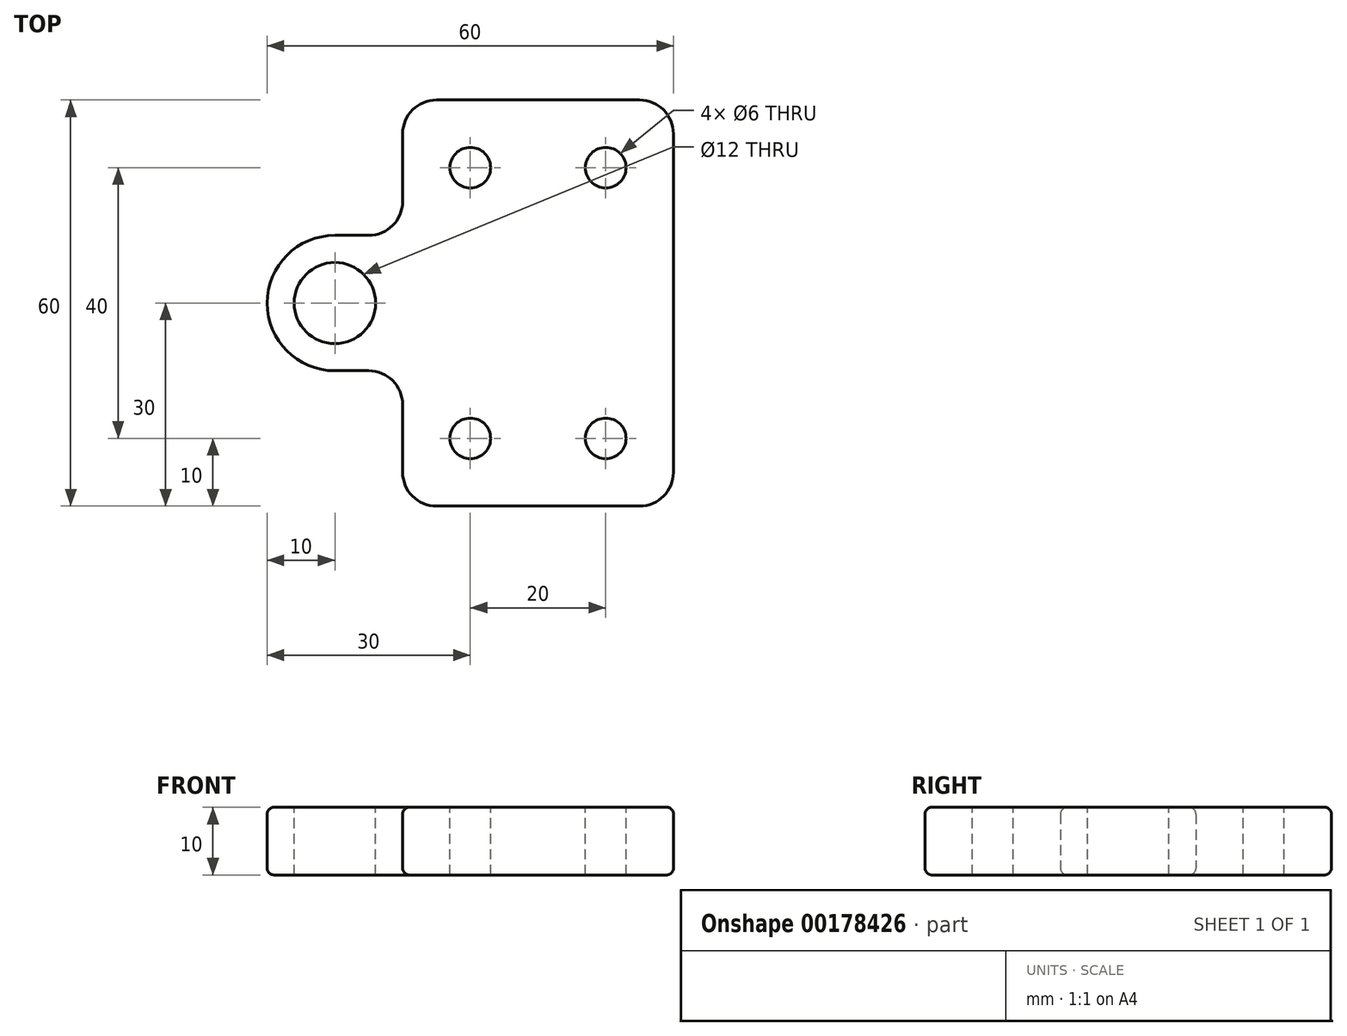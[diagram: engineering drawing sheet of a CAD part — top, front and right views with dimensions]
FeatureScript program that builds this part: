
annotation { "Feature Type Name" : "Feature", "Feature Type Description" : "" }
export const myFeature = defineFeature(function(context is Context, id is Id, definition is map)
    precondition{}
    {
        {
            var Q0;
            Q0=qCreatedBy(makeId("Top.planeOp"),FACE);
            var sketch = newSketch(context, id + "F0", { "sketchPlane" : qUnion([Q0])});
            skLineSegment(sketch, "E0.bottom", {"start": v(-20, 30) * mm, "end": v(20, 30) * mm});
            skLineSegment(sketch, "E0.top", {"start": v(-20, -30) * mm, "end": v(20, -30) * mm});
            skLineSegment(sketch, "E0.left", {"start": v(-20, 30) * mm, "end": v(-20, 10) * mm});
            skLineSegment(sketch, "E0.right", {"start": v(20, 30) * mm, "end": v(20, -30) * mm});
            skPoint(sketch, "E0.middle", {"position": v(0, 0) * mm});
            skPoint(sketch, "E1", {"position": v(-30, 0) * mm});
            skPoint(sketch, "E1.positionSnap0", {"position": v(-20, 0) * mm});
            skArc(sketch, "E2", {"start": v(-30, 10) * mm, "mid": v(-40, 0) * mm, "end": v(-30, -10) * mm});
            skLineSegment(sketch, "E3", {"start": v(-30, 10) * mm, "end": v(-20, 10) * mm});
            skLineSegment(sketch, "E4", {"start": v(-30, -10) * mm, "end": v(-20, -10) * mm});
            skLineSegment(sketch, "E5.trimOffspring", {"start": v(-20, -10) * mm, "end": v(-20, -30) * mm});
            skSolve(sketch);
        }
        {
            var Q0;
            Q0=makeQuery(id+"F0.imprint","IMPRINT",FACE,{"disambiguationData":[TD([[makeQuery(id+"F0.imprint","IMPRINT",EDGE,{"derivedFrom":sQuery(id+"F0.wireOp",EDGE,"E0.bottom")}),-1.0]])]});
            extrude(context, id + "F1", {"entities" : qUnion([Q0]), "depth" : 10 * mm});
        }
        {
            var Q0;
            Q0=makeQuery(id+"F1.opExtrude","SWEPT_EDGE",EDGE,{"disambiguationData":[OSD([sQuery(id+"F0.wireOp",EDGE,"E0.bottom"),sQuery(id+"F0.wireOp",EDGE,"E0.left")])]});
            var Q1;
            Q1=makeQuery(id+"F1.opExtrude","SWEPT_EDGE",EDGE,{"disambiguationData":[OSD([sQuery(id+"F0.wireOp",EDGE,"E0.top"),sQuery(id+"F0.wireOp",EDGE,"E5.trimOffspring")])]});
            var Q2;
            Q2=makeQuery(id+"F1.opExtrude","SWEPT_EDGE",EDGE,{"disambiguationData":[OSD([sQuery(id+"F0.wireOp",EDGE,"E0.top"),sQuery(id+"F0.wireOp",EDGE,"E0.right")])]});
            var Q3;
            Q3=makeQuery(id+"F1.opExtrude","SWEPT_EDGE",EDGE,{"disambiguationData":[OSD([sQuery(id+"F0.wireOp",EDGE,"E0.bottom"),sQuery(id+"F0.wireOp",EDGE,"E0.right")])]});
            var Q4;
            Q4=makeQuery(id+"F1.opExtrude","SWEPT_EDGE",EDGE,{"disambiguationData":[OSD([sQuery(id+"F0.wireOp",EDGE,"E4"),sQuery(id+"F0.wireOp",EDGE,"E5.trimOffspring")])]});
            var Q5;
            Q5=makeQuery(id+"F1.opExtrude","SWEPT_EDGE",EDGE,{"disambiguationData":[OSD([sQuery(id+"F0.wireOp",EDGE,"E0.left"),sQuery(id+"F0.wireOp",EDGE,"E3")])]});
            fillet(context, id + "F2", {"entities" : qUnion([Q0, Q1, Q2, Q3, Q4, Q5]), "radius" : 5 * mm, "tangentPropagation" : true, "allowEdgeOverflow" : false});
        }
        {
            var Q0;
            Q0=makeQuery(id+"F1.opExtrude","CAP_FACE",FACE,{"disambiguationData":[OSD([sQuery(id+"F0.wireOp",EDGE,"E0.bottom"),sQuery(id+"F0.wireOp",EDGE,"E0.top"),sQuery(id+"F0.wireOp",EDGE,"E0.left"),sQuery(id+"F0.wireOp",EDGE,"E0.right"),sQuery(id+"F0.wireOp",EDGE,"E2"),sQuery(id+"F0.wireOp",EDGE,"E3"),sQuery(id+"F0.wireOp",EDGE,"E4"),sQuery(id+"F0.wireOp",EDGE,"E5.trimOffspring")])],"isStart":false});
            var sketch = newSketch(context, id + "F3", { "sketchPlane" : qUnion([Q0])});
            skPoint(sketch, "E6", {"position": v(-10, 20) * mm});
            skLineSegment(sketch, "E7", {"start": v(0, 37.64) * mm, "end": v(0, -37.85) * mm, "construction": true});
            skLineSegment(sketch, "E8", {"start": v(-47.1, 0) * mm, "end": v(28.56, 0) * mm, "construction": true});
            skPoint(sketch, "E9.MirrorP", {"position": v(10, 20) * mm});
            skLineSegment(sketch, "E10.MirrorCS", {"start": v(47.1, 0) * mm, "end": v(-28.56, 0) * mm, "construction": true});
            skPoint(sketch, "E11.MirrorP", {"position": v(-10, -20) * mm});
            skPoint(sketch, "E12.MirrorP", {"position": v(10, -20) * mm});
            skSolve(sketch);
        }
        {
            var Q0;
            Q0=sQuery(id+"F3.wireOp",VERTEX,"E6");
            var Q1;
            Q1=sQuery(id+"F3.wireOp",VERTEX,"E9.MirrorP");
            var Q2;
            Q2=sQuery(id+"F3.wireOp",VERTEX,"E12.MirrorP");
            var Q3;
            Q3=sQuery(id+"F3.wireOp",VERTEX,"E11.MirrorP");
            var Q4;
            Q4=makeQuery(id+"F1.opExtrude","SWEPT_BODY",BODY,{"disambiguationData":[OSD([sQuery(id+"F0.wireOp",EDGE,"E0.bottom"),sQuery(id+"F0.wireOp",EDGE,"E0.top"),sQuery(id+"F0.wireOp",EDGE,"E0.left"),sQuery(id+"F0.wireOp",EDGE,"E0.right"),sQuery(id+"F0.wireOp",EDGE,"E2"),sQuery(id+"F0.wireOp",EDGE,"E3"),sQuery(id+"F0.wireOp",EDGE,"E4"),sQuery(id+"F0.wireOp",EDGE,"E5.trimOffspring")])]});
            hole(context, id + "F4", {"style" : HoleStyle.SIMPLE, "endStyle" : HoleEndStyle.THROUGH, "holeDiameter" : 6 * mm, "locations" : qUnion([Q0, Q1, Q2, Q3]), "scope" : qUnion([Q4]), "isTappedThrough" : true});
        }
        {
            var Q0;
            Q0=makeQuery(id+"F1.opExtrude","CAP_FACE",FACE,{"disambiguationData":[OSD([sQuery(id+"F0.wireOp",EDGE,"E0.bottom"),sQuery(id+"F0.wireOp",EDGE,"E0.top"),sQuery(id+"F0.wireOp",EDGE,"E0.left"),sQuery(id+"F0.wireOp",EDGE,"E0.right"),sQuery(id+"F0.wireOp",EDGE,"E2"),sQuery(id+"F0.wireOp",EDGE,"E3"),sQuery(id+"F0.wireOp",EDGE,"E4"),sQuery(id+"F0.wireOp",EDGE,"E5.trimOffspring")])],"isStart":false});
            var sketch = newSketch(context, id + "F5", { "sketchPlane" : qUnion([Q0])});
            skPoint(sketch, "E13", {"position": v(-30, 0) * mm});
            skPoint(sketch, "E14", {"position": v(-95.19, 13.6) * mm});
            skSolve(sketch);
        }
        {
            var Q0;
            Q0=sQuery(id+"F5.wireOp",VERTEX,"E13");
            var Q1;
            Q1=makeQuery(id+"F1.opExtrude","SWEPT_BODY",BODY,{"disambiguationData":[OSD([sQuery(id+"F0.wireOp",EDGE,"E0.bottom"),sQuery(id+"F0.wireOp",EDGE,"E0.top"),sQuery(id+"F0.wireOp",EDGE,"E0.left"),sQuery(id+"F0.wireOp",EDGE,"E0.right"),sQuery(id+"F0.wireOp",EDGE,"E2"),sQuery(id+"F0.wireOp",EDGE,"E3"),sQuery(id+"F0.wireOp",EDGE,"E4"),sQuery(id+"F0.wireOp",EDGE,"E5.trimOffspring")])]});
            hole(context, id + "F6", {"style" : HoleStyle.SIMPLE, "endStyle" : HoleEndStyle.THROUGH, "holeDiameter" : 12 * mm, "locations" : qUnion([Q0]), "scope" : qUnion([Q1]), "isTappedThrough" : true});
        }
        {
            var Q0;
            Q0=makeQuery(id+"F1.opExtrude","CAP_EDGE",EDGE,{"disambiguationData":[OSD([sQuery(id+"F0.wireOp",EDGE,"E0.bottom")])],"isStart":true});
            var Q1;
            Q1=makeQuery(id+"F1.opExtrude","CAP_EDGE",EDGE,{"disambiguationData":[OSD([sQuery(id+"F0.wireOp",EDGE,"E0.bottom")])],"isStart":false});
            fillet(context, id + "F7", {"entities" : qUnion([Q0, Q1]), "radius" : 1 * mm, "tangentPropagation" : true, "allowEdgeOverflow" : false});
        }
    });
